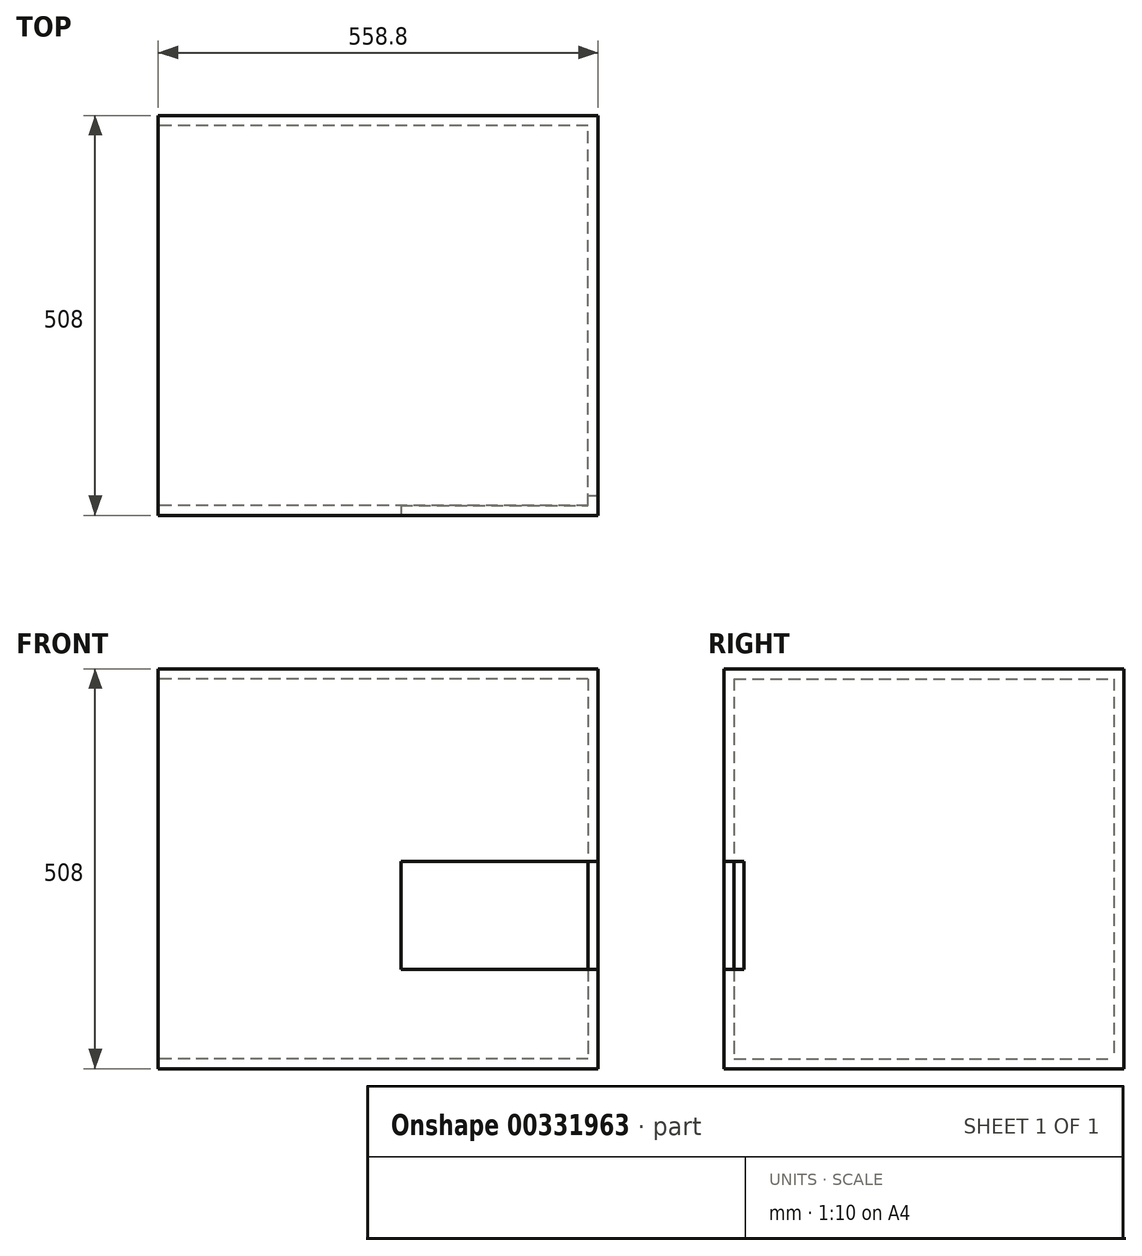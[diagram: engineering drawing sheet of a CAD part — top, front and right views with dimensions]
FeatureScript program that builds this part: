
annotation { "Feature Type Name" : "Feature", "Feature Type Description" : "" }
export const myFeature = defineFeature(function(context is Context, id is Id, definition is map)
    precondition{}
    {
        {
            var Q0;
            Q0=qCreatedBy(makeId("Front.planeOp"),FACE);
            var sketch = newSketch(context, id + "F0", { "sketchPlane" : qUnion([Q0])});
            skLineSegment(sketch, "E0.bottom", {"start": v(0, -74.6) * mm, "end": v(-558.8, -74.6) * mm});
            skLineSegment(sketch, "E0.top", {"start": v(0, -582.6) * mm, "end": v(-558.8, -582.6) * mm});
            skLineSegment(sketch, "E0.left", {"start": v(0, -74.6) * mm, "end": v(0, -582.6) * mm});
            skLineSegment(sketch, "E0.right", {"start": v(-558.8, -74.6) * mm, "end": v(-558.8, -582.6) * mm});
            skSolve(sketch);
        }
        {
            var Q0;
            Q0=makeQuery(id+"F0.imprint","IMPRINT",FACE,{"disambiguationData":[TD([[makeQuery(id+"F0.imprint","IMPRINT",EDGE,{"derivedFrom":sQuery(id+"F0.wireOp",EDGE,"E0.bottom")}),1.0]])]});
            extrude(context, id + "F1", {"entities" : qUnion([Q0]), "depth" : 508 * mm});
        }
        {
            var Q0;
            Q0=makeQuery(id+"F1.opExtrude","SWEPT_FACE",FACE,{"disambiguationData":[OSD([sQuery(id+"F0.wireOp",EDGE,"E0.right")])]});
            shell(context, id + "F2", {"entities" : qUnion([Q0]), "thickness" : 12.7 * mm});
        }
        {
            var Q0;
            Q0=makeQuery(id+"F1.opExtrude","CAP_FACE",FACE,{"disambiguationData":[OSD([sQuery(id+"F0.wireOp",EDGE,"E0.bottom"),sQuery(id+"F0.wireOp",EDGE,"E0.top"),sQuery(id+"F0.wireOp",EDGE,"E0.left"),sQuery(id+"F0.wireOp",EDGE,"E0.right")])],"isStart":false});
            var sketch = newSketch(context, id + "F3", { "sketchPlane" : qUnion([Q0])});
            skLineSegment(sketch, "E1", {"start": v(0, -462.94) * mm, "end": v(-257.02, -462.94) * mm});
            skLineSegment(sketch, "E2", {"start": v(-257.02, -462.94) * mm, "end": v(-257.02, -312.96) * mm});
            skLineSegment(sketch, "E3", {"start": v(-257.02, -312.96) * mm, "end": v(0, -312.96) * mm});
            skSolve(sketch);
        }
        {
            var Q0;
            Q0=sQuery(id+"F3.wireOp",EDGE,"E1");
            var Q1;
            Q1=sQuery(id+"F3.wireOp",EDGE,"E2");
            var Q2;
            Q2=sQuery(id+"F3.wireOp",EDGE,"E3");
            extrude(context, id + "F4", {"bodyType" : ToolBodyType.SURFACE, "surfaceEntities" : qUnion([Q0, Q1, Q2]), "depth" : 50.8 * mm});
        }
        {
            var Q0;
            Q0=makeQuery(id+"F1.opExtrude","CAP_FACE",FACE,{"disambiguationData":[OSD([sQuery(id+"F0.wireOp",EDGE,"E0.bottom"),sQuery(id+"F0.wireOp",EDGE,"E0.top"),sQuery(id+"F0.wireOp",EDGE,"E0.left"),sQuery(id+"F0.wireOp",EDGE,"E0.right")])],"isStart":false});
            var sketch = newSketch(context, id + "F5", { "sketchPlane" : qUnion([Q0])});
            skLineSegment(sketch, "E4.0", {"start": v(-250.67, -456.6) * mm, "end": v(0, -456.6) * mm});
            skLineSegment(sketch, "E4.1", {"start": v(-250.67, -319.31) * mm, "end": v(-250.67, -456.6) * mm});
            skLineSegment(sketch, "E4.2", {"start": v(0, -319.31) * mm, "end": v(-250.67, -319.31) * mm});
            skLineSegment(sketch, "E5", {"start": v(0, -456.6) * mm, "end": v(0, -319.31) * mm});
            skSolve(sketch);
        }
        {
            var Q0;
            Q0=makeQuery(id+"F5.imprint","IMPRINT",FACE,{"disambiguationData":[TD([[makeQuery(id+"F5.imprint","IMPRINT",EDGE,{"derivedFrom":sQuery(id+"F5.wireOp",EDGE,"E4.0")}),1.0]])]});
            extrude(context, id + "F6", {"entities" : qUnion([Q0]), "operationType" : NewBodyOperationType.REMOVE, "oppositeDirection" : true, "depth" : 25.4 * mm});
        }
    });
